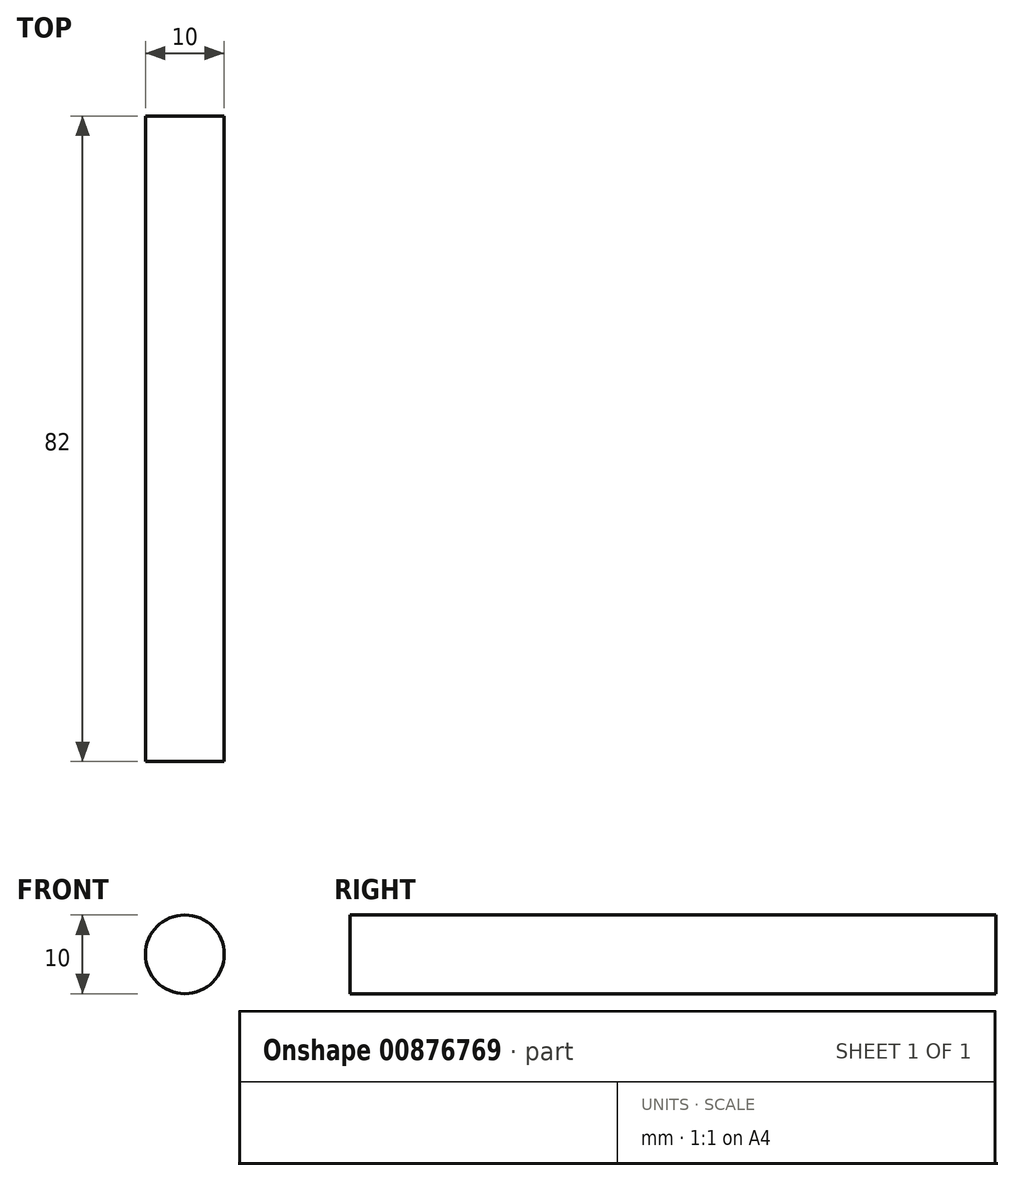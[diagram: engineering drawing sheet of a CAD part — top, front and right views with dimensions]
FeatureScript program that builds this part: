
annotation { "Feature Type Name" : "Feature", "Feature Type Description" : "" }
export const myFeature = defineFeature(function(context is Context, id is Id, definition is map)
    precondition{}
    {
        {
            var Q0;
            Q0=qCreatedBy(makeId("Front.planeOp"),FACE);
            var sketch = newSketch(context, id + "F0", { "sketchPlane" : qUnion([Q0])});
            skCircle(sketch, "E0", {"center": v(0, 0) * mm, "radius": 5 * mm});
            skSolve(sketch);
        }
        {
            var Q0;
            Q0=qSketchRegion(id+"F0",true);
            extrude(context, id + "F1", {"entities" : qUnion([Q0]), "depth" : 82 * mm, "offsetDistance" : 25 * mm});
        }
    });
